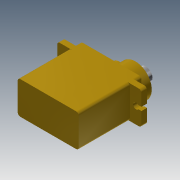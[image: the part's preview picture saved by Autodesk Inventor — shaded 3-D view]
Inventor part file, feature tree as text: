
AUTODESK INVENTOR PART (.ipt)
format: ipt  version: 2015 (Build 190159000, 159)  size: 225,792 bytes
history: native  units: mm
features: sketch x18, fillet x12, extrude x11
ambient origin geometry x8: Origin, YZ Plane, XZ Plane, XY Plane, X Axis, Y Axis, Z Axis, Center Point
bodies: Solid1 (feature_tree)
feature tree (41):
  extrude  "Extrusion1"  Depth=4.4mm TaperAngle=0.0deg
  sketch  "Sketch2"  dims[d11=4.4mm d12=0.0mm d18=7.9mm d19=0.0mm]
  sketch  "Sketch6"  dims[d20=7.9mm d21=0.0mm d22=7.9mm d23=0.0mm]
  extrude  "Extrusion2"  Depth=7.9mm TaperAngle=0.0deg
  sketch  "Sketch7"  dims[d26=4.0mm d27=0.0mm d28=5.0mm]
  sketch  "Sketch8"  dims[d29=3.0mm d30=0.0mm d31=3.0mm d32=0.0mm]
  sketch  "Sketch9"  dims[d39=3.0mm d40=0.0mm d43=3.0mm d44=0.0mm]
  extrude  "Extrusion3"  Depth=7.9mm TaperAngle=0.0deg
  sketch  "Sketch10"  dims[d45=1.0mm d46=1.0mm]
  sketch  "Sketch11"  dims[d47=1.0mm d48=1.0mm]
  extrude  "Extrusion4"  Depth=4.0mm
  extrude  "Extrusion5"  Depth=3.0mm TaperAngle=0.0deg
  extrude  "Extrusion6"  Depth=3.0mm TaperAngle=0.0deg
  extrude  "Extrusion7"  Depth=1.0mm
  extrude  "Extrusion8"  Depth=1.0mm
  extrude  "Extrusion9"  Depth=1.0mm
  sketch  "Sketch16"
  sketch  "Sketch17"
  sketch  "Sketch18"
  sketch  "Sketch19"
  extrude  "Extrusion10"  Depth=1.0mm
  extrude  "Extrusion11"  Depth=1.0mm
  fillet  "Fillet1"  Radius=1.0mm
  sketch  "Sketch20"
  fillet  "Fillet2"  Radius=1.0mm
  fillet  "Fillet3"  [1 undecoded]
  fillet  "Fillet4"  [1 undecoded]
  fillet  "Fillet5"  [1 undecoded]
  fillet  "Fillet6"  [1 undecoded]
  fillet  "Fillet7"  [1 undecoded]
  fillet  "Fillet8"  [1 undecoded]
  fillet  "Fillet9"  [1 undecoded]
  fillet  "Fillet10"  [1 undecoded]
  fillet  "Fillet11"  [1 undecoded]
  fillet  "Fillet12"  [1 undecoded]
  sketch  "Sketch21"
  sketch  "Sketch1"  dims[d2=31.7mm d3=0.0mm d7=4.4mm d8=0.0mm]
  sketch  "Sketch12"  dims[d49=1.0mm d50=1.0mm]
  sketch  "Sketch13"  dims[d51=1.0mm d52=1.0mm]
  sketch  "Sketch14"  dims[d53=1.0mm d54=1.0mm d55=1.0mm d56=1.0mm]
  sketch  "Sketch15"
note: 10 required parameter values undecoded (feature->parameter linkage not recoverable at this tier; creation-order binding heuristic only, values carry confidence <= 0.55)
